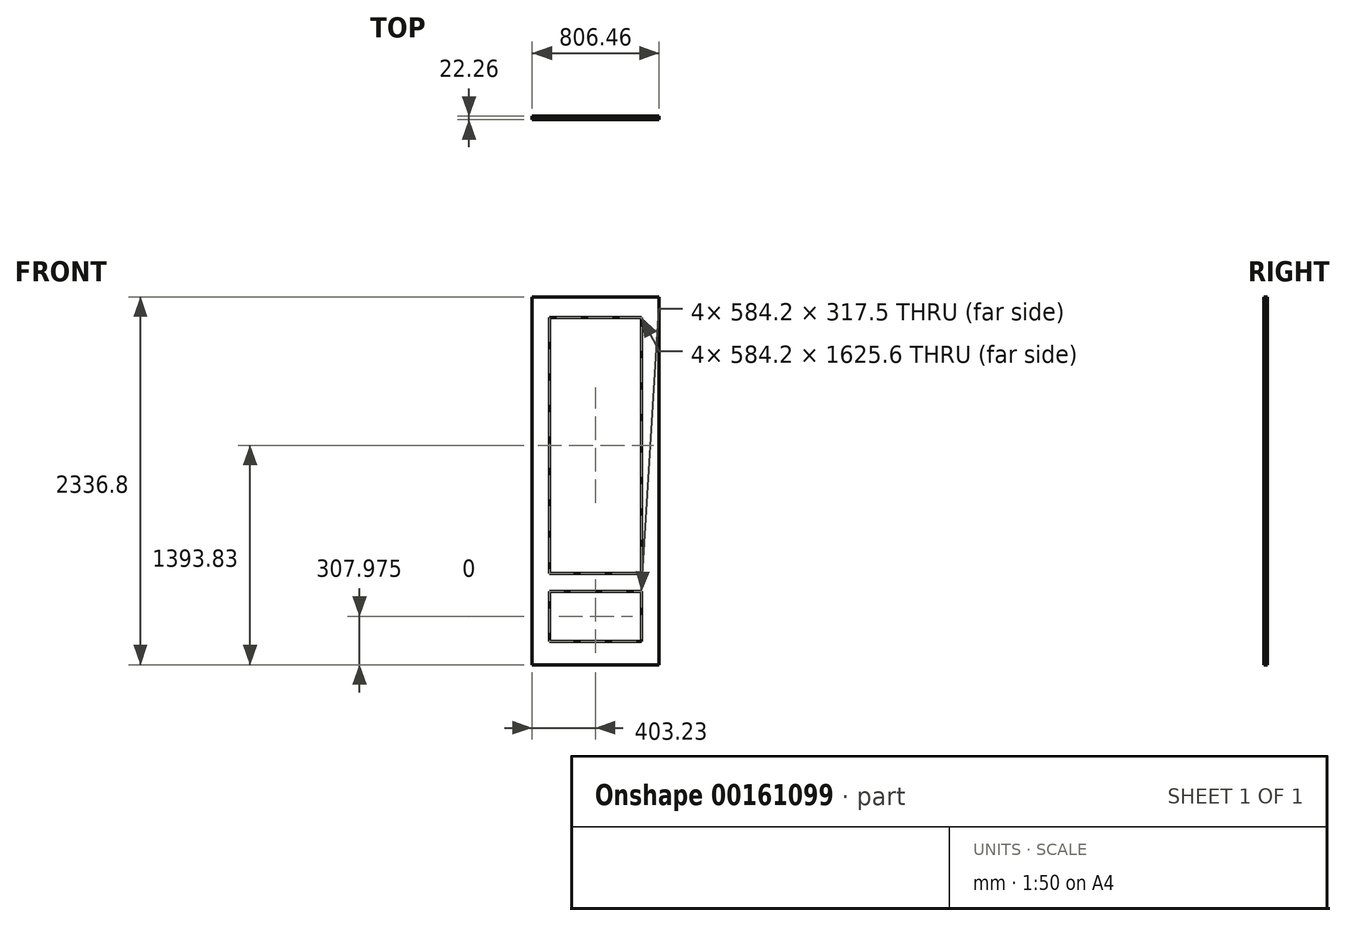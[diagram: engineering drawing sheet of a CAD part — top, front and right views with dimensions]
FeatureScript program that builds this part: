
annotation { "Feature Type Name" : "Feature", "Feature Type Description" : "" }
export const myFeature = defineFeature(function(context is Context, id is Id, definition is map)
    precondition{}
    {
        {
            var Q0;
            Q0=qCreatedBy(makeId("Front.planeOp"),FACE);
            var sketch = newSketch(context, id + "F0", { "sketchPlane" : qUnion([Q0])});
            skLineSegment(sketch, "E0.bottom", {"start": v(403.23, 1206.5) * mm, "end": v(-403.23, 1206.5) * mm});
            skLineSegment(sketch, "E0.top", {"start": v(403.23, -1206.5) * mm, "end": v(-403.23, -1206.5) * mm});
            skLineSegment(sketch, "E0.left", {"start": v(403.23, 1206.5) * mm, "end": v(403.23, -1206.5) * mm});
            skLineSegment(sketch, "E0.right", {"start": v(-403.23, 1206.5) * mm, "end": v(-403.23, -1206.5) * mm});
            skPoint(sketch, "E0.middle", {"position": v(0, 0) * mm});
            skLineSegment(sketch, "E1.bottom", {"start": v(-292.1, -663.58) * mm, "end": v(292.1, -663.58) * mm});
            skLineSegment(sketch, "E1.top", {"start": v(-292.1, -981.08) * mm, "end": v(292.1, -981.08) * mm});
            skLineSegment(sketch, "E1.left", {"start": v(-292.1, -663.58) * mm, "end": v(-292.1, -981.08) * mm});
            skLineSegment(sketch, "E1.right", {"start": v(292.1, -663.58) * mm, "end": v(292.1, -981.08) * mm});
            skLineSegment(sketch, "E2.bottom", {"start": v(-292.1, 1076.33) * mm, "end": v(292.1, 1076.33) * mm});
            skLineSegment(sketch, "E2.top", {"start": v(-292.1, -549.27) * mm, "end": v(292.1, -549.27) * mm});
            skLineSegment(sketch, "E2.left", {"start": v(-292.1, 1076.33) * mm, "end": v(-292.1, -549.27) * mm});
            skLineSegment(sketch, "E2.right", {"start": v(292.1, 1076.33) * mm, "end": v(292.1, -549.27) * mm});
            skSolve(sketch);
        }
        {
            var Q0;
            Q0 = qSketchRegion(id + "F0", true);
            extrude(context, id + "F1", {"entities" : qUnion([Q0]), "depth" : 22.22 * mm, "hasSecondDirection" : true, "secondDirectionOppositeDirection" : true, "secondDirectionDepth" : 1.75 / 50.8 * mm});
        }
        {
            var Q0;
            Q0=qCreatedBy(makeId("Front.planeOp"),FACE);
            var sketch = newSketch(context, id + "F2", { "sketchPlane" : qUnion([Q0])});
            skLineSegment(sketch, "E3.bottom", {"start": v(-561.43, 1477.6) * mm, "end": v(687.16, 1477.6) * mm});
            skLineSegment(sketch, "E3.top", {"start": v(-561.43, 1206.5) * mm, "end": v(687.16, 1206.5) * mm});
            skLineSegment(sketch, "E3.left", {"start": v(-561.43, 1477.6) * mm, "end": v(-561.43, 1206.5) * mm});
            skLineSegment(sketch, "E3.right", {"start": v(687.16, 1477.6) * mm, "end": v(687.16, 1206.5) * mm});
            skLineSegment(sketch, "E4.bottom", {"start": v(687.16, -1130.3) * mm, "end": v(-561.43, -1130.3) * mm});
            skLineSegment(sketch, "E4.top", {"start": v(687.16, -1634.32) * mm, "end": v(-561.43, -1634.32) * mm});
            skLineSegment(sketch, "E4.left", {"start": v(687.16, -1130.3) * mm, "end": v(687.16, -1634.32) * mm});
            skLineSegment(sketch, "E4.right", {"start": v(-561.43, -1130.3) * mm, "end": v(-561.43, -1634.32) * mm});
            skSolve(sketch);
        }
        {
            var Q0;
            Q0 = qSketchRegion(id + "F2", true);
            extrude(context, id + "F3", {"entities" : qUnion([Q0]), "operationType" : NewBodyOperationType.REMOVE, "endBound" : BoundingType.THROUGH_ALL, "oppositeDirection" : true, "depth" : 25.4 * mm, "hasSecondDirection" : true, "secondDirectionBound" : SecondDirectionBoundingType.THROUGH_ALL, "secondDirectionOppositeDirection" : false, "secondDirectionDepth" : 25.4 * mm});
        }
    });
